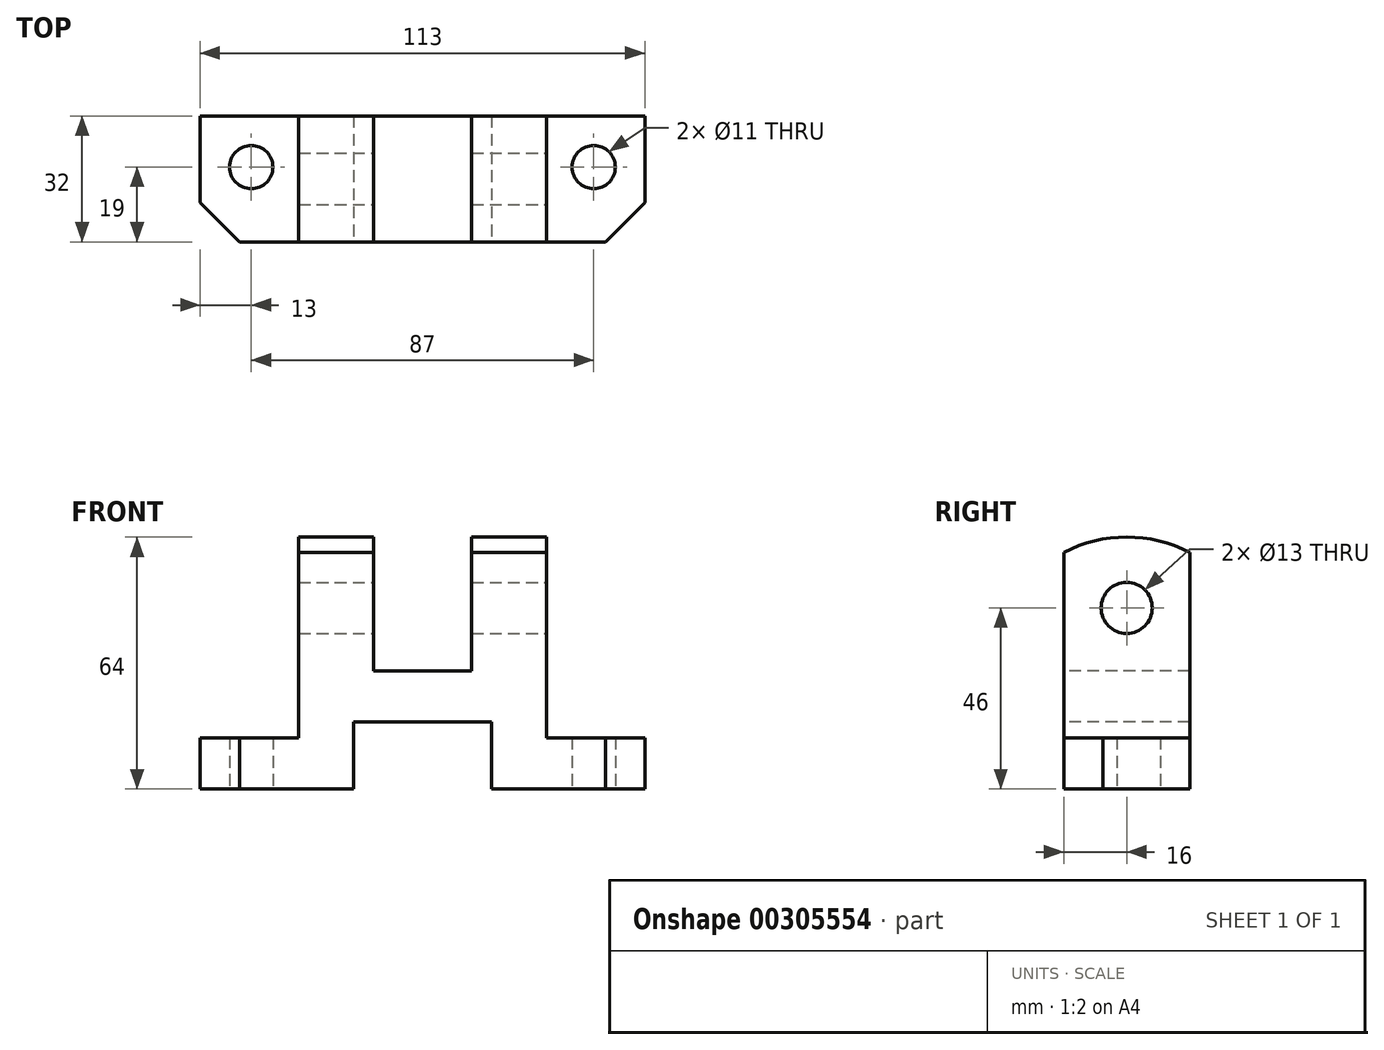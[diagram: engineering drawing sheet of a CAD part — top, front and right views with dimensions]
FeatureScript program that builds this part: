
annotation { "Feature Type Name" : "Feature", "Feature Type Description" : "" }
export const myFeature = defineFeature(function(context is Context, id is Id, definition is map)
    precondition{}
    {
        {
            var Q0;
            Q0=qCreatedBy(makeId("Right.planeOp"),FACE);
            var sketch = newSketch(context, id + "F0", { "sketchPlane" : qUnion([Q0])});
            skLineSegment(sketch, "E0", {"start": v(-16, 60.13) * mm, "end": v(-16, 0) * mm});
            skLineSegment(sketch, "E1", {"start": v(-16, 0) * mm, "end": v(16, 0) * mm});
            skLineSegment(sketch, "E2", {"start": v(16, 0) * mm, "end": v(16, 60.13) * mm});
            skArc(sketch, "E3", {"start": v(16, 60.13) * mm, "mid": v(0, 64) * mm, "end": v(-16, 60.13) * mm});
            skSolve(sketch);
        }
        {
            var Q0;
            Q0 = qSketchRegion(id + "F0", true);
            extrude(context, id + "F1", {"entities" : qUnion([Q0]), "depth" : 113 * mm});
        }
        {
            var Q0;
            Q0=makeQuery(id+"F1.opExtrude","CAP_FACE",FACE,{"disambiguationData":[OSD([sQuery(id+"F0.wireOp",EDGE,"E0"),sQuery(id+"F0.wireOp",EDGE,"E1"),sQuery(id+"F0.wireOp",EDGE,"E2"),sQuery(id+"F0.wireOp",EDGE,"E3")])],"isStart":false});
            var sketch = newSketch(context, id + "F2", { "sketchPlane" : qUnion([Q0])});
            skCircle(sketch, "E4", {"center": v(0, 46) * mm, "radius": 6.5 * mm});
            skSolve(sketch);
        }
        {
            var Q0;
            Q0 = qSketchRegion(id + "F2", true);
            extrude(context, id + "F3", {"entities" : qUnion([Q0]), "operationType" : NewBodyOperationType.REMOVE, "endBound" : BoundingType.THROUGH_ALL, "oppositeDirection" : true, "depth" : 25 * mm});
        }
        {
            var Q0;
            Q0=makeQuery(id+"F1.opExtrude","SWEPT_FACE",FACE,{"disambiguationData":[OSD([sQuery(id+"F0.wireOp",EDGE,"E0")])]});
            var sketch = newSketch(context, id + "F4", { "sketchPlane" : qUnion([Q0])});
            skLineSegment(sketch, "E5.bottom", {"start": v(0, 64) * mm, "end": v(25, 64) * mm});
            skLineSegment(sketch, "E5.top", {"start": v(0, 13) * mm, "end": v(25, 13) * mm});
            skLineSegment(sketch, "E5.left", {"start": v(0, 64) * mm, "end": v(0, 13) * mm});
            skLineSegment(sketch, "E5.right", {"start": v(25, 64) * mm, "end": v(25, 13) * mm});
            skLineSegment(sketch, "E6.bottom", {"start": v(113, 64) * mm, "end": v(88, 64) * mm});
            skLineSegment(sketch, "E6.top", {"start": v(113, 13) * mm, "end": v(88, 13) * mm});
            skLineSegment(sketch, "E6.left", {"start": v(113, 64) * mm, "end": v(113, 13) * mm});
            skLineSegment(sketch, "E6.right", {"start": v(88, 64) * mm, "end": v(88, 13) * mm});
            skSolve(sketch);
        }
        {
            var Q0;
            Q0 = qSketchRegion(id + "F4", true);
            extrude(context, id + "F5", {"entities" : qUnion([Q0]), "operationType" : NewBodyOperationType.REMOVE, "endBound" : BoundingType.THROUGH_ALL, "oppositeDirection" : true, "depth" : 25 * mm});
        }
        {
            var Q0;
            Q0=makeQuery(id+"F1.opExtrude","SWEPT_FACE",FACE,{"disambiguationData":[OSD([sQuery(id+"F0.wireOp",EDGE,"E0")])]});
            var sketch = newSketch(context, id + "F6", { "sketchPlane" : qUnion([Q0])});
            skLineSegment(sketch, "E7.bottom", {"start": v(44, 64) * mm, "end": v(69, 64) * mm});
            skLineSegment(sketch, "E7.top", {"start": v(44, 30) * mm, "end": v(69, 30) * mm});
            skLineSegment(sketch, "E7.left", {"start": v(44, 64) * mm, "end": v(44, 30) * mm});
            skLineSegment(sketch, "E7.right", {"start": v(69, 64) * mm, "end": v(69, 30) * mm});
            skSolve(sketch);
        }
        {
            var Q0;
            Q0 = qSketchRegion(id + "F6", true);
            extrude(context, id + "F7", {"entities" : qUnion([Q0]), "operationType" : NewBodyOperationType.REMOVE, "endBound" : BoundingType.THROUGH_ALL, "oppositeDirection" : true, "depth" : 25 * mm});
        }
        {
            var Q0;
            Q0=makeQuery(id+"F1.opExtrude","SWEPT_FACE",FACE,{"disambiguationData":[OSD([sQuery(id+"F0.wireOp",EDGE,"E0")])]});
            var sketch = newSketch(context, id + "F8", { "sketchPlane" : qUnion([Q0])});
            skLineSegment(sketch, "E8.bottom", {"start": v(39, 0) * mm, "end": v(74, 0) * mm});
            skLineSegment(sketch, "E8.top", {"start": v(39, 17) * mm, "end": v(74, 17) * mm});
            skLineSegment(sketch, "E8.left", {"start": v(39, 0) * mm, "end": v(39, 17) * mm});
            skLineSegment(sketch, "E8.right", {"start": v(74, 0) * mm, "end": v(74, 17) * mm});
            skSolve(sketch);
        }
        {
            var Q0;
            Q0 = qSketchRegion(id + "F8", true);
            extrude(context, id + "F9", {"entities" : qUnion([Q0]), "operationType" : NewBodyOperationType.REMOVE, "endBound" : BoundingType.THROUGH_ALL, "oppositeDirection" : true, "depth" : 25 * mm});
        }
        {
            var Q0;
            Q0=qCreatedBy(makeId("Top.planeOp"),FACE);
            var sketch = newSketch(context, id + "F10", { "sketchPlane" : qUnion([Q0])});
            skCircle(sketch, "E9", {"center": v(13, 3) * mm, "radius": 5.5 * mm});
            skCircle(sketch, "E10", {"center": v(100, 3) * mm, "radius": 5.5 * mm});
            skLineSegment(sketch, "E11", {"start": v(0, -6) * mm, "end": v(10, -16) * mm});
            skLineSegment(sketch, "E12", {"start": v(10, -16) * mm, "end": v(0, -16) * mm});
            skLineSegment(sketch, "E13", {"start": v(0, -16) * mm, "end": v(0, -6) * mm});
            skLineSegment(sketch, "E14", {"start": v(113, -6) * mm, "end": v(103, -16) * mm});
            skLineSegment(sketch, "E15", {"start": v(103, -16) * mm, "end": v(113, -16) * mm});
            skLineSegment(sketch, "E16", {"start": v(113, -16) * mm, "end": v(113, -6) * mm});
            skSolve(sketch);
        }
        {
            var Q0;
            Q0 = qSketchRegion(id + "F10", true);
            extrude(context, id + "F11", {"entities" : qUnion([Q0]), "operationType" : NewBodyOperationType.REMOVE, "endBound" : BoundingType.THROUGH_ALL, "depth" : 25 * mm});
        }
    });
